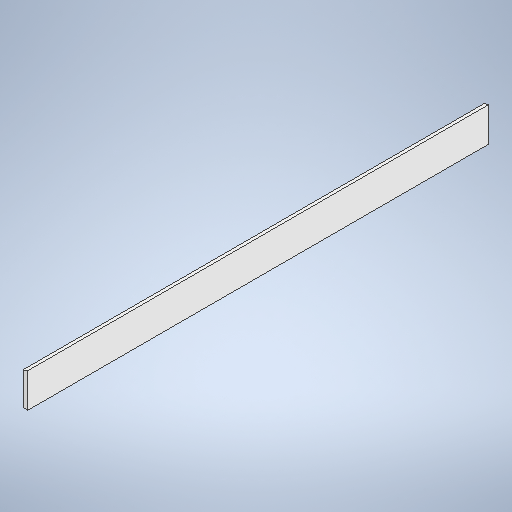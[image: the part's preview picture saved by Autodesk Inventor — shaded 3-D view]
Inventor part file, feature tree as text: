
AUTODESK INVENTOR PART (.ipt)
format: ipt  version: 2025 (Build 290162010, 162A)  size: 249,344 bytes
history: native  units: in
note: dims shown in document units (in); Inventor stores cm internally (conversion verified against a paired STEP export)
features: extrude x1, sketch x1
ambient origin geometry x8: Origin, YZ Plane, XZ Plane, XY Plane, X Axis, Y Axis, Z Axis, Center Point
bodies: Body1 (feature_tree)
feature tree (2):
  extrude  "Extrusion3"  Depth=97.504in
  sketch  "Sketch1"  dims[d33=42.875in d36=132.0in d37=3.5in d42=1.0in d43=7.25in d44=97.504in d45=0.0in]
